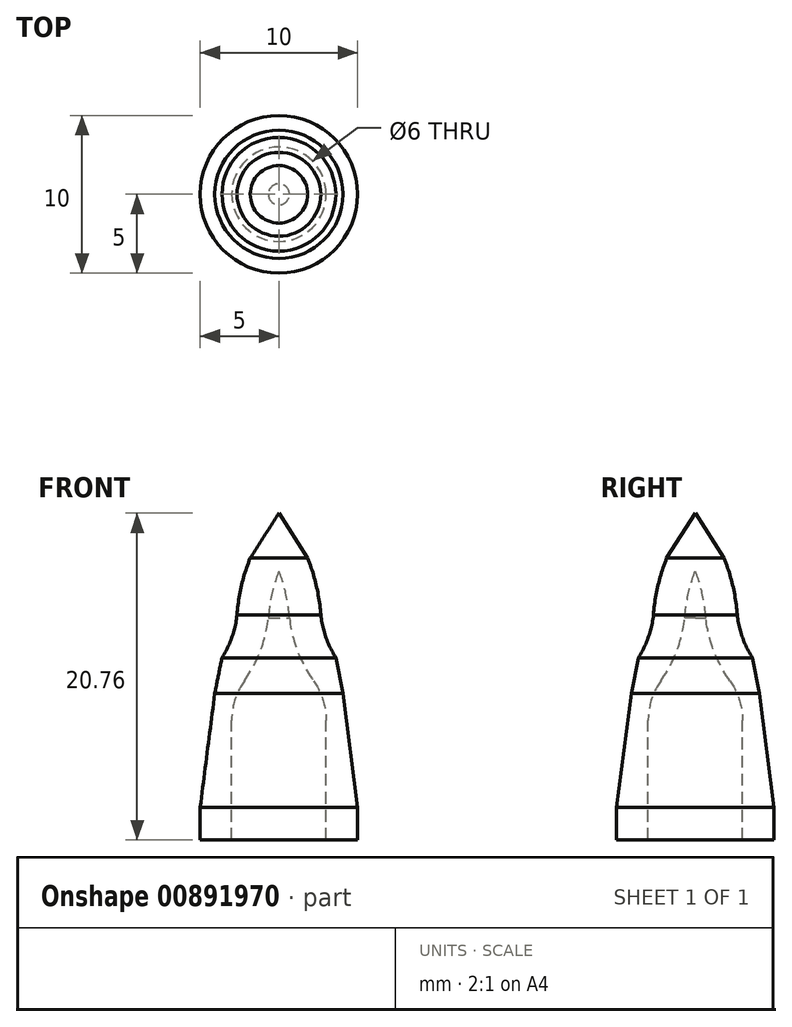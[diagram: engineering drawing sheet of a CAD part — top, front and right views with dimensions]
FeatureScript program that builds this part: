
annotation { "Feature Type Name" : "Feature", "Feature Type Description" : "" }
export const myFeature = defineFeature(function(context is Context, id is Id, definition is map)
    precondition{}
    {
        {
            var Q0;
            Q0=qCreatedBy(makeId("Front.planeOp"),FACE);
            var sketch = newSketch(context, id + "F0", { "sketchPlane" : qUnion([Q0])});
            skLineSegment(sketch, "E0", {"start": v(5, 0) * mm, "end": v(5, 2.07) * mm});
            skArc(sketch, "E1", {"start": v(2.66, 14.28) * mm, "mid": v(3.05, 12.7) * mm, "end": v(3.82, 11.26) * mm});
            skArc(sketch, "E2", {"start": v(2.66, 14.28) * mm, "mid": v(1.85, 17.82) * mm, "end": v(0, 20.95) * mm});
            skPoint(sketch, "E3.visualSharp", {"position": v(5, 10) * mm});
            skArc(sketch, "E4.0", {"start": v(0.67, 14.1) * mm, "mid": v(0.45, 15.6) * mm, "end": v(0, 17.07) * mm});
            skArc(sketch, "E4.1", {"start": v(0.67, 14.1) * mm, "mid": v(1.18, 12) * mm, "end": v(2.2, 10.1) * mm});
            skArc(sketch, "E4.2", {"start": v(3, 7.58) * mm, "mid": v(2.8, 8.9) * mm, "end": v(2.2, 10.1) * mm});
            skLineSegment(sketch, "E4.3", {"start": v(3, 0) * mm, "end": v(3, 7.58) * mm});
            skLineSegment(sketch, "E5", {"start": v(0, 20.95) * mm, "end": v(0, 12.4) * mm});
            skLineSegment(sketch, "E6", {"start": v(3, 0) * mm, "end": v(5, 0) * mm});
            skLineSegment(sketch, "E7", {"start": v(3.82, 11.26) * mm, "end": v(5, 2.07) * mm});
            skSolve(sketch);
        }
        {
            var Q0;
            Q0=makeQuery(id+"F0.imprint","IMPRINT",FACE,{"disambiguationData":[TD([[makeQuery(id+"F0.imprint","IMPRINT",EDGE,{"derivedFrom":sQuery(id+"F0.wireOp",EDGE,"E0")}),1.0]])]});
            var Q1;
            Q1=sQuery(id+"F0.wireOp",EDGE,"E5");
            revolve(context, id + "F1", {"surfaceOperationType" : NewSurfaceOperationType.NEW, "entities" : qUnion([Q0]), "axis" : qUnion([Q1]), "revolveType" : RevolveType.FULL});
        }
        {
            var Q0;
            Q0=qCreatedBy(makeId("Front.planeOp"),FACE);
            var sketch = newSketch(context, id + "F2", { "sketchPlane" : qUnion([Q0])});
            skLineSegment(sketch, "E8", {"start": v(0, 21.91) * mm, "end": v(0, 20.76) * mm});
            skLineSegment(sketch, "E9", {"start": v(0, 20.76) * mm, "end": v(3.3, 15.59) * mm});
            skLineSegment(sketch, "E10", {"start": v(3.3, 15.59) * mm, "end": v(3.3, 13.16) * mm});
            skLineSegment(sketch, "E11", {"start": v(3.3, 13.16) * mm, "end": v(5.52, 2.16) * mm});
            skLineSegment(sketch, "E12", {"start": v(5.52, 2.16) * mm, "end": v(9.9, 13.37) * mm});
            skLineSegment(sketch, "E13", {"start": v(9.9, 13.37) * mm, "end": v(0, 21.91) * mm});
            skSolve(sketch);
        }
        {
            var Q0;
            Q0 = qSketchRegion(id + "F2", true);
            var Q1;
            Q1=sQuery(id+"F2.wireOp",EDGE,"E8");
            revolve(context, id + "F3", {"operationType" : NewBodyOperationType.REMOVE, "surfaceOperationType" : NewSurfaceOperationType.NEW, "entities" : qUnion([Q0]), "axis" : qUnion([Q1]), "revolveType" : RevolveType.FULL, "oppositeDirection" : true});
        }
    });
